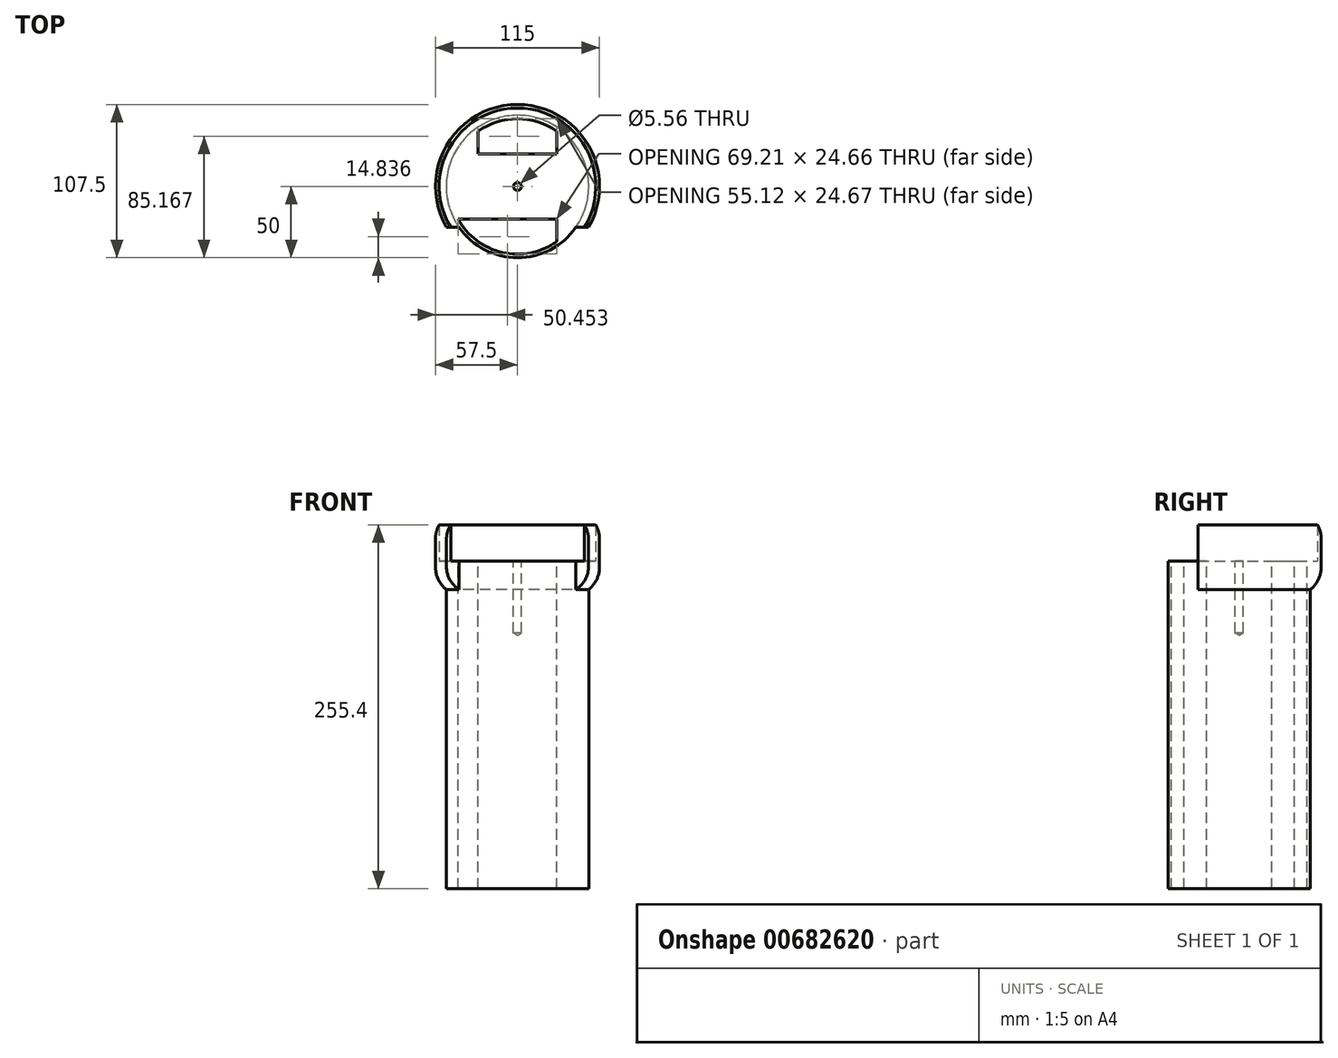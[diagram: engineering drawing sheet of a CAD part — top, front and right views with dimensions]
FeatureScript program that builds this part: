
annotation { "Feature Type Name" : "Feature", "Feature Type Description" : "" }
export const myFeature = defineFeature(function(context is Context, id is Id, definition is map)
    precondition{}
    {
        {
            var Q0;
            Q0=qCreatedBy(makeId("Top.planeOp"),FACE);
            var sketch = newSketch(context, id + "F0", { "sketchPlane" : qUnion([Q0])});
            skCircle(sketch, "E0", {"center": v(0, 0) * mm, "radius": 50 * mm});
            skSolve(sketch);
        }
        {
            var Q0;
            Q0=makeQuery(id+"F0.imprint","IMPRINT",FACE,{"disambiguationData":[TD([[makeQuery(id+"F0.imprint","IMPRINT",EDGE,{"derivedFrom":sQuery(id+"F0.wireOp",EDGE,"E0")}),1.0]])]});
            extrude(context, id + "F1", {"entities" : qUnion([Q0]), "depth" : 210 * mm, "offsetDistance" : 25 * mm});
        }
        {
            var Q0;
            Q0=makeQuery(id+"F1.opExtrude","CAP_FACE",FACE,{"disambiguationData":[OSD([sQuery(id+"F0.wireOp",EDGE,"E0")])],"isStart":false});
            var sketch = newSketch(context, id + "F2", { "sketchPlane" : qUnion([Q0])});
            skPoint(sketch, "E1", {"position": v(0, 0) * mm});
            skSolve(sketch);
        }
        {
            var Q0;
            Q0=sQuery(id+"F2.wireOp",VERTEX,"E1");
            var Q1;
            Q1=makeQuery(id+"F1.opExtrude","SWEPT_BODY",BODY,{"disambiguationData":[OSD([sQuery(id+"F0.wireOp",EDGE,"E0")])]});
            hole(context, id + "F3", {"style" : HoleStyle.SIMPLE, "endStyle" : HoleEndStyle.BLIND, "standardTappedOrClearance" : lookupTablePath({ "standard" : "ANSI", "engagement" : "50%", "pitch" : "20 tpi", "size" : "1/4", "type" : "Tapped" }), "standardBlindInLast" : lookupTablePath({ "standard" : "ANSI", "engagement" : "50%", "pitch" : "20 tpi", "size" : "1/4", "type" : "Tapped" }), "holeDiameter" : 5.56 * mm, "majorDiameter" : 6.35 * mm, "showTappedDepth" : true, "holeDepth" : 30.48 * mm, "isTappedThrough" : true, "tappedDepth" : 25.4 * mm, "tapClearance" : 4, "locations" : qUnion([Q0]), "scope" : qUnion([Q1])});
        }
        {
            var Q0;
            Q0=makeQuery(id+"F1.opExtrude","CAP_FACE",FACE,{"disambiguationData":[OSD([sQuery(id+"F0.wireOp",EDGE,"E0")])],"isStart":false});
            var sketch = newSketch(context, id + "F4", { "sketchPlane" : qUnion([Q0])});
            skCircle(sketch, "E2", {"center": v(0, 0) * mm, "radius": 57.5 * mm});
            skSolve(sketch);
        }
        {
            var Q0;
            Q0=makeQuery(id+"F4.imprint","IMPRINT",FACE,{"disambiguationData":[TD([[makeQuery(id+"F4.imprint","IMPRINT",EDGE,{"derivedFrom":sQuery(id+"F4.wireOp",EDGE,"E2")}),1.0]])]});
            var Q1;
            Q1=makeQuery(id+"F4.imprint","IMPRINT",FACE,{"disambiguationData":[TD([[makeQuery(id+"F4.imprint","IMPRINT",EDGE,{"derivedFrom":makeQuery(id+"F1.opExtrude","CAP_EDGE",EDGE,{"disambiguationData":[OSD([sQuery(id+"F0.wireOp",EDGE,"E0")])],"isStart":false})}),1.0]])]});
            extrude(context, id + "F5", {"entities" : qUnion([Q0, Q1]), "operationType" : NewBodyOperationType.ADD, "depth" : 20 * mm, "offsetDistance" : 25 * mm});
        }
        {
            var Q0;
            Q0=makeQuery(id+"F5.opExtrude","CAP_FACE",FACE,{"disambiguationData":[OSD([sQuery(id+"F3.hole-0.sketch.wireOp",EDGE,"core_line_2"),sQuery(id+"F3.hole-0.sketch.wireOp",EDGE,"core_line_3"),sQuery(id+"F4.wireOp",EDGE,"E2")])],"isStart":false});
            var sketch = newSketch(context, id + "F6", { "sketchPlane" : qUnion([Q0])});
            skCircle(sketch, "E3", {"center": v(0, 0) * mm, "radius": 55 * mm});
            skCircle(sketch, "E4.0.0", {"center": v(0, 0) * mm, "radius": 57.5 * mm});
            skSolve(sketch);
        }
        {
            var Q0;
            Q0=makeQuery(id+"F6.imprint","IMPRINT",FACE,{"disambiguationData":[TD([[makeQuery(id+"F6.imprint","IMPRINT",EDGE,{"derivedFrom":sQuery(id+"F6.wireOp",EDGE,"E3")}),-1.0]])]});
            extrude(context, id + "F7", {"entities" : qUnion([Q0]), "operationType" : NewBodyOperationType.ADD, "depth" : 25.4 * mm, "offsetDistance" : 25 * mm});
        }
        {
            var Q0;
            Q0=makeQuery(id+"F7.opExtrude","CAP_EDGE",EDGE,{"disambiguationData":[OSD([sQuery(id+"F6.wireOp",EDGE,"E4.0.0")])],"isStart":false});
            fillet(context, id + "F8", {"entities" : qUnion([Q0]), "radius" : 20 * mm, "tangentPropagation" : true, "allowEdgeOverflow" : false});
        }
        {
            var Q0;
            Q0=makeQuery(id+"F5.opExtrude","CAP_EDGE",EDGE,{"disambiguationData":[OSD([sQuery(id+"F4.wireOp",EDGE,"E2")])],"isStart":true});
            fillet(context, id + "F9", {"entities" : qUnion([Q0]), "radius" : 20 * mm, "tangentPropagation" : true, "allowEdgeOverflow" : false});
        }
        {
            var Q0;
            Q0=makeQuery(id+"F5.opExtrude","CAP_FACE",FACE,{"disambiguationData":[OSD([sQuery(id+"F3.hole-0.sketch.wireOp",EDGE,"core_line_2"),sQuery(id+"F3.hole-0.sketch.wireOp",EDGE,"core_line_3"),sQuery(id+"F4.wireOp",EDGE,"E2")])],"isStart":false});
            var sketch = newSketch(context, id + "F10", { "sketchPlane" : qUnion([Q0])});
            skLineSegment(sketch, "E5.bottom", {"start": v(-27.56, -22.83) * mm, "end": v(27.56, -22.83) * mm});
            skLineSegment(sketch, "E5.top", {"start": v(-27.56, 22.83) * mm, "end": v(27.56, 22.83) * mm});
            skLineSegment(sketch, "E5.left", {"start": v(-27.56, -22.83) * mm, "end": v(-27.56, 22.83) * mm});
            skLineSegment(sketch, "E5.right", {"start": v(27.56, -22.83) * mm, "end": v(27.56, 22.83) * mm});
            skPoint(sketch, "E5.middle", {"position": v(0, 0) * mm});
            skCircle(sketch, "E6", {"center": v(0, 0) * mm, "radius": 47.5 * mm});
            skLineSegment(sketch, "E7", {"start": v(-27.56, -22.83) * mm, "end": v(-41.65, -22.83) * mm});
            skLineSegment(sketch, "E8", {"start": v(27.56, -22.83) * mm, "end": v(27.56, -38.69) * mm});
            skLineSegment(sketch, "E9", {"start": v(-27.56, 22.83) * mm, "end": v(-27.56, 38.69) * mm});
            skLineSegment(sketch, "E10", {"start": v(27.56, 22.83) * mm, "end": v(27.56, 38.69) * mm});
            skSolve(sketch);
        }
        {
            var Q0;
            Q0=makeQuery(id+"F10.imprint","IMPRINT",FACE,{"disambiguationData":[TD([[makeQuery(id+"F10.imprint","IMPRINT",EDGE,{"derivedFrom":sQuery(id+"F10.wireOp",EDGE,"E5.top")}),1.0]])]});
            var Q1;
            Q1=makeQuery(id+"F10.imprint","IMPRINT",FACE,{"disambiguationData":[TD([[makeQuery(id+"F10.imprint","IMPRINT",EDGE,{"derivedFrom":sQuery(id+"F10.wireOp",EDGE,"E5.bottom")}),-1.0]])]});
            extrude(context, id + "F11", {"entities" : qUnion([Q0, Q1]), "operationType" : NewBodyOperationType.REMOVE, "endBound" : BoundingType.THROUGH_ALL, "oppositeDirection" : true, "depth" : 25 * mm, "offsetDistance" : 25 * mm});
        }
        {
            var Q0;
            Q0=makeQuery(id+"F1.opExtrude","CAP_FACE",FACE,{"disambiguationData":[OSD([sQuery(id+"F0.wireOp",EDGE,"E0")])],"isStart":true});
            var sketch = newSketch(context, id + "F12", { "sketchPlane" : qUnion([Q0])});
            skCircle(sketch, "E11.0.0", {"center": v(0, 0) * mm, "radius": 50 * mm});
            skArc(sketch, "E12.0", {"start": v(-41.65, 22.83) * mm, "mid": v(-10.6, 46.3) * mm, "end": v(27.56, 38.69) * mm});
            skSolve(sketch);
        }
        {
            var Q0;
            Q0=makeQuery(id+"F4.imprint","IMPRINT",FACE,{"disambiguationData":[TD([[makeQuery(id+"F4.imprint","IMPRINT",EDGE,{"derivedFrom":makeQuery(id+"F1.opExtrude","CAP_EDGE",EDGE,{"disambiguationData":[OSD([sQuery(id+"F0.wireOp",EDGE,"E0")])],"isStart":false})}),1.0]])]});
            var sketch = newSketch(context, id + "F13", { "sketchPlane" : qUnion([Q0])});
            skArc(sketch, "E13", {"start": v(-49.8, -28.75) * mm, "mid": v(0, -57.5) * mm, "end": v(49.8, -28.75) * mm});
            skLineSegment(sketch, "E14", {"start": v(-49.8, -28.75) * mm, "end": v(49.8, -28.75) * mm});
            skSolve(sketch);
        }
        {
            var Q0;
            {var subQ0=sQuery(id+"F13.wireOp",EDGE,"E13");Q0=makeQuery(id+"F13.imprint","IMPRINT",FACE,{"disambiguationData":[TD([[makeQuery(id+"F13.imprint","IMPRINT",EDGE,{"derivedFrom":subQ0}),1.0]])]});}
            extrude(context, id + "F14", {"entities" : qUnion([Q0]), "operationType" : NewBodyOperationType.REMOVE, "endBound" : BoundingType.THROUGH_ALL, "depth" : 25 * mm, "offsetDistance" : 25 * mm});
        }
        {
            var Q0;
            Q0=qCreatedBy(makeId("Top.planeOp"),FACE);
            cPlane(context, id + "F15", {"entities" : qUnion([Q0]), "cplaneType" : CPlaneType.OFFSET, "offset" : 210 * mm, "width" : 150 * mm, "height" : 150 * mm});
        }
    });
